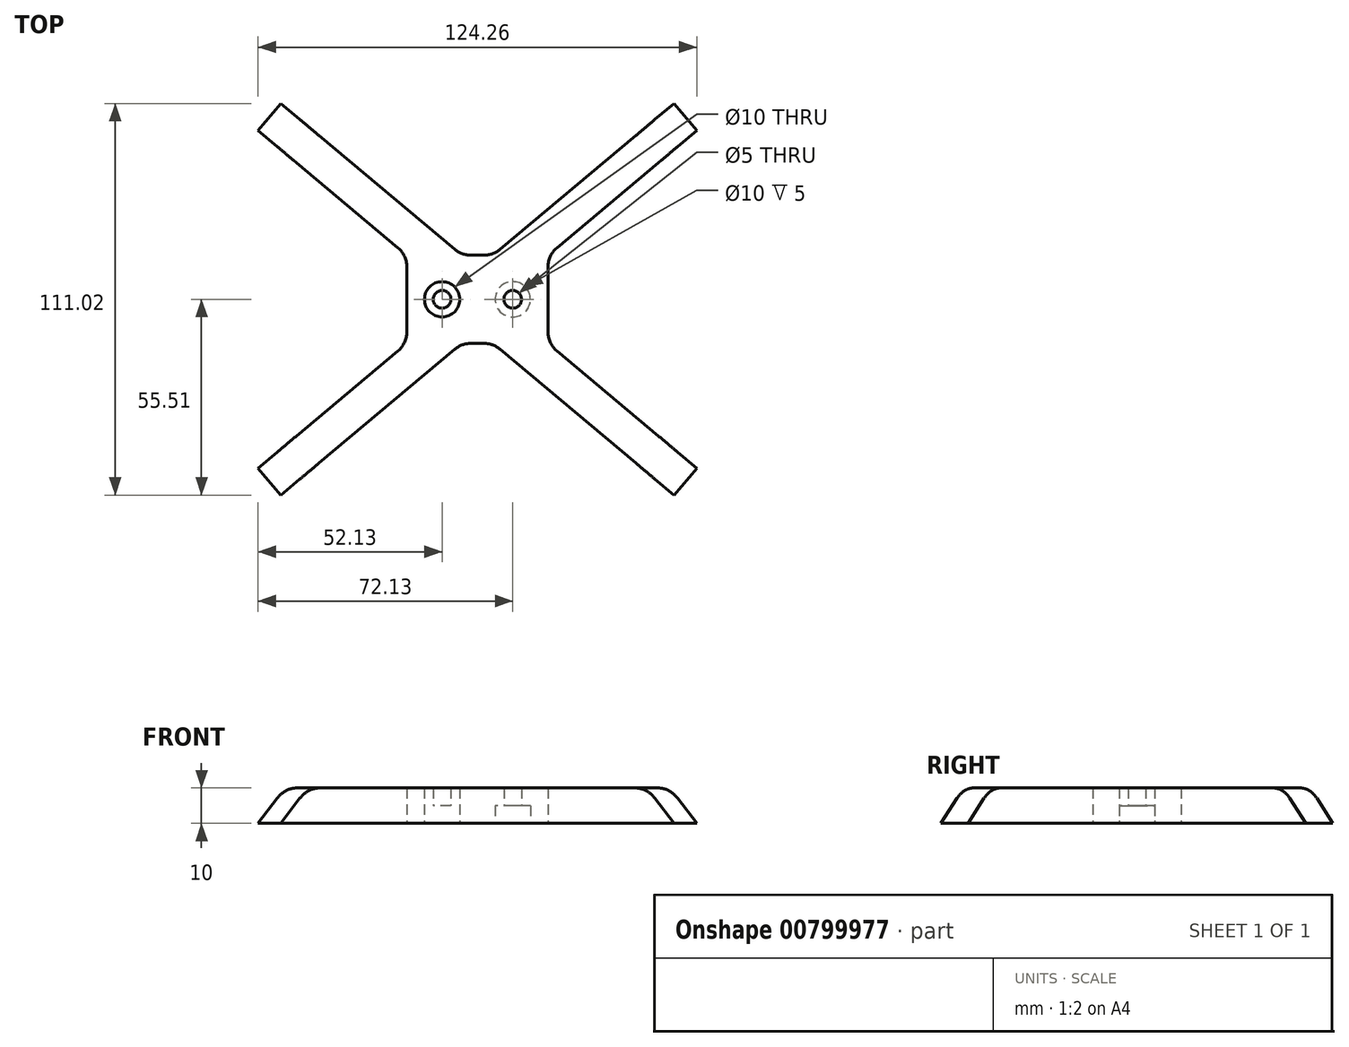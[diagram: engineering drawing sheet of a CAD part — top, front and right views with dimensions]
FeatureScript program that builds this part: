
annotation { "Feature Type Name" : "Feature", "Feature Type Description" : "" }
export const myFeature = defineFeature(function(context is Context, id is Id, definition is map)
    precondition{}
    {
        {
            var Q0;
            Q0=qCreatedBy(makeId("Top.planeOp"),FACE);
            var sketch = newSketch(context, id + "F0", { "sketchPlane" : qUnion([Q0])});
            skLineSegment(sketch, "E0.bottom", {"start": v(20, -12.5) * mm, "end": v(-20, -12.5) * mm});
            skLineSegment(sketch, "E0.top", {"start": v(20, 12.5) * mm, "end": v(-20, 12.5) * mm});
            skLineSegment(sketch, "E0.left", {"start": v(20, -12.5) * mm, "end": v(20, 12.5) * mm});
            skLineSegment(sketch, "E0.right", {"start": v(-20, -12.5) * mm, "end": v(-20, 12.5) * mm});
            skPoint(sketch, "E0.middle", {"position": v(0, 0) * mm});
            skLineSegment(sketch, "E1", {"start": v(4.44, 12.5) * mm, "end": v(55.7, 55.51) * mm});
            skLineSegment(sketch, "E2", {"start": v(55.7, 55.51) * mm, "end": v(62.13, 47.85) * mm});
            skLineSegment(sketch, "E3", {"start": v(62.13, 47.85) * mm, "end": v(20, 12.5) * mm});
            skLineSegment(sketch, "E4.MirrorCS", {"start": v(55.7, -55.51) * mm, "end": v(62.13, -47.85) * mm});
            skLineSegment(sketch, "E5.MirrorCS", {"start": v(62.13, -47.85) * mm, "end": v(20, -12.5) * mm});
            skLineSegment(sketch, "E6.MirrorCS", {"start": v(4.44, -12.5) * mm, "end": v(55.7, -55.51) * mm});
            skLineSegment(sketch, "E7.MirrorCS", {"start": v(-55.7, -55.51) * mm, "end": v(-62.13, -47.85) * mm});
            skLineSegment(sketch, "E8.MirrorCS", {"start": v(-4.44, -12.5) * mm, "end": v(-55.7, -55.51) * mm});
            skLineSegment(sketch, "E9.MirrorCS", {"start": v(-62.13, -47.85) * mm, "end": v(-20, -12.5) * mm});
            skLineSegment(sketch, "E10.MirrorCS", {"start": v(-55.7, 55.51) * mm, "end": v(-62.13, 47.85) * mm});
            skLineSegment(sketch, "E11.MirrorCS", {"start": v(-4.44, 12.5) * mm, "end": v(-55.7, 55.51) * mm});
            skLineSegment(sketch, "E12.MirrorCS", {"start": v(-62.13, 47.85) * mm, "end": v(-20, 12.5) * mm});
            skCircle(sketch, "E13", {"center": v(10, 0) * mm, "radius": 5 * mm});
            skCircle(sketch, "E14", {"center": v(10, 0) * mm, "radius": 2.5 * mm});
            skCircle(sketch, "E15.MirrorC", {"center": v(-10, 0) * mm, "radius": 2.5 * mm});
            skCircle(sketch, "E16.MirrorC", {"center": v(-10, 0) * mm, "radius": 5 * mm});
            skSolve(sketch);
        }
        {
            var Q0;
            {var subQ0=sQuery(id+"F0.wireOp",EDGE,"E0.left");Q0=makeQuery(id+"F0.imprint","IMPRINT",FACE,{"disambiguationData":[TD([[makeQuery(id+"F0.imprint","IMPRINT",EDGE,{"derivedFrom":subQ0}),1.0]])]});}
            var Q1;
            Q1=makeQuery(id+"F0.imprint","IMPRINT",FACE,{"disambiguationData":[TD([[makeQuery(id+"F0.imprint","IMPRINT",EDGE,{"derivedFrom":sQuery(id+"F0.wireOp",EDGE,"E7.MirrorCS")}),-1.0]])]});
            var Q2;
            Q2=makeQuery(id+"F0.imprint","IMPRINT",FACE,{"disambiguationData":[TD([[makeQuery(id+"F0.imprint","IMPRINT",EDGE,{"derivedFrom":sQuery(id+"F0.wireOp",EDGE,"E4.MirrorCS")}),1.0]])]});
            var Q3;
            {var subQ2=sQuery(id+"F0.wireOp",EDGE,"E1");Q3=makeQuery(id+"F0.imprint","IMPRINT",FACE,{"disambiguationData":[TD([[makeQuery(id+"F0.imprint","IMPRINT",EDGE,{"derivedFrom":subQ2}),-1.0]])]});}
            var Q4;
            Q4=makeQuery(id+"F0.imprint","IMPRINT",FACE,{"disambiguationData":[TD([[makeQuery(id+"F0.imprint","IMPRINT",EDGE,{"derivedFrom":sQuery(id+"F0.wireOp",EDGE,"E10.MirrorCS")}),1.0]])]});
            var Q5;
            Q5=makeQuery(id+"F0.imprint","IMPRINT",FACE,{"disambiguationData":[TD([[makeQuery(id+"F0.imprint","IMPRINT",EDGE,{"derivedFrom":sQuery(id+"F0.wireOp",EDGE,"E13")}),1.0]])]});
            var Q6;
            Q6=makeQuery(id+"F0.imprint","IMPRINT",FACE,{"disambiguationData":[TD([[makeQuery(id+"F0.imprint","IMPRINT",EDGE,{"derivedFrom":sQuery(id+"F0.wireOp",EDGE,"E15.MirrorC")}),1.0]])]});
            extrude(context, id + "F1", {"entities" : qUnion([Q0, Q1, Q2, Q3, Q4, Q5, Q6]), "depth" : 10 * mm, "offsetDistance" : 25 * mm});
        }
        {
            var Q0;
            Q0=makeQuery(id+"F0.imprint","IMPRINT",FACE,{"disambiguationData":[TD([[makeQuery(id+"F0.imprint","IMPRINT",EDGE,{"derivedFrom":sQuery(id+"F0.wireOp",EDGE,"E15.MirrorC")}),1.0]])]});
            var Q1;
            Q1=makeQuery(id+"F0.imprint","IMPRINT",FACE,{"disambiguationData":[TD([[makeQuery(id+"F0.imprint","IMPRINT",EDGE,{"derivedFrom":sQuery(id+"F0.wireOp",EDGE,"E13")}),1.0]])]});
            extrude(context, id + "F2", {"entities" : qUnion([Q0, Q1]), "operationType" : NewBodyOperationType.REMOVE, "depth" : 5 * mm, "offsetDistance" : 25 * mm});
        }
        {
            var Q0;
            Q0=makeQuery(id+"F1.opExtrude","CAP_EDGE",EDGE,{"disambiguationData":[OSD([sQuery(id+"F0.wireOp",EDGE,"E4.MirrorCS")])],"isStart":false});
            var Q1;
            Q1=makeQuery(id+"F1.opExtrude","CAP_EDGE",EDGE,{"disambiguationData":[OSD([sQuery(id+"F0.wireOp",EDGE,"E2")])],"isStart":false});
            var Q2;
            Q2=makeQuery(id+"F1.opExtrude","CAP_EDGE",EDGE,{"disambiguationData":[OSD([sQuery(id+"F0.wireOp",EDGE,"E10.MirrorCS")])],"isStart":false});
            var Q3;
            Q3=makeQuery(id+"F1.opExtrude","CAP_EDGE",EDGE,{"disambiguationData":[OSD([sQuery(id+"F0.wireOp",EDGE,"E7.MirrorCS")])],"isStart":false});
            chamfer(context, id + "F3", {"entities" : qUnion([Q0, Q1, Q2, Q3]), "width" : 10 * mm, "tangentPropagation" : true});
        }
        {
            var Q0;
            Q0=makeQuery(id+"F1.opExtrude","SWEPT_EDGE",EDGE,{"disambiguationData":[OSD([sQuery(id+"F0.wireOp",EDGE,"E0.top"),sQuery(id+"F0.wireOp",EDGE,"E1")])]});
            var Q1;
            Q1=makeQuery(id+"F1.opExtrude","SWEPT_EDGE",EDGE,{"disambiguationData":[OSD([sQuery(id+"F0.wireOp",EDGE,"E0.top"),sQuery(id+"F0.wireOp",EDGE,"E11.MirrorCS")])]});
            var Q2;
            Q2=makeQuery(id+"F1.opExtrude","SWEPT_EDGE",EDGE,{"disambiguationData":[OSD([sQuery(id+"F0.wireOp",EDGE,"E0.bottom"),sQuery(id+"F0.wireOp",EDGE,"E6.MirrorCS")])]});
            var Q3;
            Q3=makeQuery(id+"F1.opExtrude","SWEPT_EDGE",EDGE,{"disambiguationData":[OSD([sQuery(id+"F0.wireOp",EDGE,"E0.bottom"),sQuery(id+"F0.wireOp",EDGE,"E8.MirrorCS")])]});
            var Q4;
            Q4=makeQuery(id+"F1.opExtrude","SWEPT_EDGE",EDGE,{"disambiguationData":[OSD([sQuery(id+"F0.wireOp",EDGE,"E0.bottom"),sQuery(id+"F0.wireOp",EDGE,"E0.right"),sQuery(id+"F0.wireOp",EDGE,"E9.MirrorCS")])]});
            var Q5;
            Q5=makeQuery(id+"F1.opExtrude","SWEPT_EDGE",EDGE,{"disambiguationData":[OSD([sQuery(id+"F0.wireOp",EDGE,"E0.top"),sQuery(id+"F0.wireOp",EDGE,"E0.right"),sQuery(id+"F0.wireOp",EDGE,"E12.MirrorCS")])]});
            var Q6;
            Q6=makeQuery(id+"F1.opExtrude","SWEPT_EDGE",EDGE,{"disambiguationData":[OSD([sQuery(id+"F0.wireOp",EDGE,"E0.bottom"),sQuery(id+"F0.wireOp",EDGE,"E0.left"),sQuery(id+"F0.wireOp",EDGE,"E5.MirrorCS")])]});
            var Q7;
            Q7=makeQuery(id+"F1.opExtrude","SWEPT_EDGE",EDGE,{"disambiguationData":[OSD([sQuery(id+"F0.wireOp",EDGE,"E0.top"),sQuery(id+"F0.wireOp",EDGE,"E0.left"),sQuery(id+"F0.wireOp",EDGE,"E3")])]});
            fillet(context, id + "F4", {"entities" : qUnion([Q0, Q1, Q2, Q3, Q4, Q5, Q6, Q7]), "radius" : 7 * mm, "tangentPropagation" : true, "allowEdgeOverflow" : false});
        }
        {
            var Q0;
            {var subQ0=sQuery(id+"F0.wireOp",EDGE,"E10.MirrorCS");Q0=makeQuery(id+"F3.opChamfer","BLEND_EDGE",EDGE,{"blendedFrom":[makeQuery(id+"F1.opExtrude","CAP_EDGE",EDGE,{"disambiguationData":[OSD([subQ0])],"isStart":false}),makeQuery(id+"F1.opExtrude","CAP_FACE",FACE,{"disambiguationData":[OSD([sQuery(id+"F0.wireOp",EDGE,"E0.bottom"),sQuery(id+"F0.wireOp",EDGE,"E0.top"),sQuery(id+"F0.wireOp",EDGE,"E0.left"),sQuery(id+"F0.wireOp",EDGE,"E0.right"),sQuery(id+"F0.wireOp",EDGE,"E1"),sQuery(id+"F0.wireOp",EDGE,"E2"),sQuery(id+"F0.wireOp",EDGE,"E3"),sQuery(id+"F0.wireOp",EDGE,"E4.MirrorCS"),sQuery(id+"F0.wireOp",EDGE,"E5.MirrorCS"),sQuery(id+"F0.wireOp",EDGE,"E6.MirrorCS"),sQuery(id+"F0.wireOp",EDGE,"E7.MirrorCS"),sQuery(id+"F0.wireOp",EDGE,"E8.MirrorCS"),sQuery(id+"F0.wireOp",EDGE,"E9.MirrorCS"),subQ0,sQuery(id+"F0.wireOp",EDGE,"E11.MirrorCS"),sQuery(id+"F0.wireOp",EDGE,"E12.MirrorCS"),sQuery(id+"F0.wireOp",EDGE,"E14"),sQuery(id+"F0.wireOp",EDGE,"E15.MirrorC")])],"isStart":false})],"blendedInto":[makeQuery(id+"F1.opExtrude","CAP_FACE",FACE,{"disambiguationData":[OSD([sQuery(id+"F0.wireOp",EDGE,"E0.bottom"),sQuery(id+"F0.wireOp",EDGE,"E0.top"),sQuery(id+"F0.wireOp",EDGE,"E0.left"),sQuery(id+"F0.wireOp",EDGE,"E0.right"),sQuery(id+"F0.wireOp",EDGE,"E1"),sQuery(id+"F0.wireOp",EDGE,"E2"),sQuery(id+"F0.wireOp",EDGE,"E3"),sQuery(id+"F0.wireOp",EDGE,"E4.MirrorCS"),sQuery(id+"F0.wireOp",EDGE,"E5.MirrorCS"),sQuery(id+"F0.wireOp",EDGE,"E6.MirrorCS"),sQuery(id+"F0.wireOp",EDGE,"E7.MirrorCS"),sQuery(id+"F0.wireOp",EDGE,"E8.MirrorCS"),sQuery(id+"F0.wireOp",EDGE,"E9.MirrorCS"),subQ0,sQuery(id+"F0.wireOp",EDGE,"E11.MirrorCS"),sQuery(id+"F0.wireOp",EDGE,"E12.MirrorCS"),sQuery(id+"F0.wireOp",EDGE,"E14"),sQuery(id+"F0.wireOp",EDGE,"E15.MirrorC")])],"isStart":false})]});}
            var Q1;
            {var subQ0=sQuery(id+"F0.wireOp",EDGE,"E7.MirrorCS");Q1=makeQuery(id+"F3.opChamfer","BLEND_EDGE",EDGE,{"blendedFrom":[makeQuery(id+"F1.opExtrude","CAP_EDGE",EDGE,{"disambiguationData":[OSD([subQ0])],"isStart":false}),makeQuery(id+"F1.opExtrude","CAP_FACE",FACE,{"disambiguationData":[OSD([sQuery(id+"F0.wireOp",EDGE,"E0.bottom"),sQuery(id+"F0.wireOp",EDGE,"E0.top"),sQuery(id+"F0.wireOp",EDGE,"E0.left"),sQuery(id+"F0.wireOp",EDGE,"E0.right"),sQuery(id+"F0.wireOp",EDGE,"E1"),sQuery(id+"F0.wireOp",EDGE,"E2"),sQuery(id+"F0.wireOp",EDGE,"E3"),sQuery(id+"F0.wireOp",EDGE,"E4.MirrorCS"),sQuery(id+"F0.wireOp",EDGE,"E5.MirrorCS"),sQuery(id+"F0.wireOp",EDGE,"E6.MirrorCS"),subQ0,sQuery(id+"F0.wireOp",EDGE,"E8.MirrorCS"),sQuery(id+"F0.wireOp",EDGE,"E9.MirrorCS"),sQuery(id+"F0.wireOp",EDGE,"E10.MirrorCS"),sQuery(id+"F0.wireOp",EDGE,"E11.MirrorCS"),sQuery(id+"F0.wireOp",EDGE,"E12.MirrorCS"),sQuery(id+"F0.wireOp",EDGE,"E14"),sQuery(id+"F0.wireOp",EDGE,"E15.MirrorC")])],"isStart":false})],"blendedInto":[makeQuery(id+"F1.opExtrude","CAP_FACE",FACE,{"disambiguationData":[OSD([sQuery(id+"F0.wireOp",EDGE,"E0.bottom"),sQuery(id+"F0.wireOp",EDGE,"E0.top"),sQuery(id+"F0.wireOp",EDGE,"E0.left"),sQuery(id+"F0.wireOp",EDGE,"E0.right"),sQuery(id+"F0.wireOp",EDGE,"E1"),sQuery(id+"F0.wireOp",EDGE,"E2"),sQuery(id+"F0.wireOp",EDGE,"E3"),sQuery(id+"F0.wireOp",EDGE,"E4.MirrorCS"),sQuery(id+"F0.wireOp",EDGE,"E5.MirrorCS"),sQuery(id+"F0.wireOp",EDGE,"E6.MirrorCS"),subQ0,sQuery(id+"F0.wireOp",EDGE,"E8.MirrorCS"),sQuery(id+"F0.wireOp",EDGE,"E9.MirrorCS"),sQuery(id+"F0.wireOp",EDGE,"E10.MirrorCS"),sQuery(id+"F0.wireOp",EDGE,"E11.MirrorCS"),sQuery(id+"F0.wireOp",EDGE,"E12.MirrorCS"),sQuery(id+"F0.wireOp",EDGE,"E14"),sQuery(id+"F0.wireOp",EDGE,"E15.MirrorC")])],"isStart":false})]});}
            var Q2;
            {var subQ0=sQuery(id+"F0.wireOp",EDGE,"E2");Q2=makeQuery(id+"F3.opChamfer","BLEND_EDGE",EDGE,{"blendedFrom":[makeQuery(id+"F1.opExtrude","CAP_EDGE",EDGE,{"disambiguationData":[OSD([subQ0])],"isStart":false}),makeQuery(id+"F1.opExtrude","CAP_FACE",FACE,{"disambiguationData":[OSD([sQuery(id+"F0.wireOp",EDGE,"E0.bottom"),sQuery(id+"F0.wireOp",EDGE,"E0.top"),sQuery(id+"F0.wireOp",EDGE,"E0.left"),sQuery(id+"F0.wireOp",EDGE,"E0.right"),sQuery(id+"F0.wireOp",EDGE,"E1"),subQ0,sQuery(id+"F0.wireOp",EDGE,"E3"),sQuery(id+"F0.wireOp",EDGE,"E4.MirrorCS"),sQuery(id+"F0.wireOp",EDGE,"E5.MirrorCS"),sQuery(id+"F0.wireOp",EDGE,"E6.MirrorCS"),sQuery(id+"F0.wireOp",EDGE,"E7.MirrorCS"),sQuery(id+"F0.wireOp",EDGE,"E8.MirrorCS"),sQuery(id+"F0.wireOp",EDGE,"E9.MirrorCS"),sQuery(id+"F0.wireOp",EDGE,"E10.MirrorCS"),sQuery(id+"F0.wireOp",EDGE,"E11.MirrorCS"),sQuery(id+"F0.wireOp",EDGE,"E12.MirrorCS"),sQuery(id+"F0.wireOp",EDGE,"E14"),sQuery(id+"F0.wireOp",EDGE,"E15.MirrorC")])],"isStart":false})],"blendedInto":[makeQuery(id+"F1.opExtrude","CAP_FACE",FACE,{"disambiguationData":[OSD([sQuery(id+"F0.wireOp",EDGE,"E0.bottom"),sQuery(id+"F0.wireOp",EDGE,"E0.top"),sQuery(id+"F0.wireOp",EDGE,"E0.left"),sQuery(id+"F0.wireOp",EDGE,"E0.right"),sQuery(id+"F0.wireOp",EDGE,"E1"),subQ0,sQuery(id+"F0.wireOp",EDGE,"E3"),sQuery(id+"F0.wireOp",EDGE,"E4.MirrorCS"),sQuery(id+"F0.wireOp",EDGE,"E5.MirrorCS"),sQuery(id+"F0.wireOp",EDGE,"E6.MirrorCS"),sQuery(id+"F0.wireOp",EDGE,"E7.MirrorCS"),sQuery(id+"F0.wireOp",EDGE,"E8.MirrorCS"),sQuery(id+"F0.wireOp",EDGE,"E9.MirrorCS"),sQuery(id+"F0.wireOp",EDGE,"E10.MirrorCS"),sQuery(id+"F0.wireOp",EDGE,"E11.MirrorCS"),sQuery(id+"F0.wireOp",EDGE,"E12.MirrorCS"),sQuery(id+"F0.wireOp",EDGE,"E14"),sQuery(id+"F0.wireOp",EDGE,"E15.MirrorC")])],"isStart":false})]});}
            var Q3;
            {var subQ0=sQuery(id+"F0.wireOp",EDGE,"E4.MirrorCS");Q3=makeQuery(id+"F3.opChamfer","BLEND_EDGE",EDGE,{"blendedFrom":[makeQuery(id+"F1.opExtrude","CAP_EDGE",EDGE,{"disambiguationData":[OSD([subQ0])],"isStart":false}),makeQuery(id+"F1.opExtrude","CAP_FACE",FACE,{"disambiguationData":[OSD([sQuery(id+"F0.wireOp",EDGE,"E0.bottom"),sQuery(id+"F0.wireOp",EDGE,"E0.top"),sQuery(id+"F0.wireOp",EDGE,"E0.left"),sQuery(id+"F0.wireOp",EDGE,"E0.right"),sQuery(id+"F0.wireOp",EDGE,"E1"),sQuery(id+"F0.wireOp",EDGE,"E2"),sQuery(id+"F0.wireOp",EDGE,"E3"),subQ0,sQuery(id+"F0.wireOp",EDGE,"E5.MirrorCS"),sQuery(id+"F0.wireOp",EDGE,"E6.MirrorCS"),sQuery(id+"F0.wireOp",EDGE,"E7.MirrorCS"),sQuery(id+"F0.wireOp",EDGE,"E8.MirrorCS"),sQuery(id+"F0.wireOp",EDGE,"E9.MirrorCS"),sQuery(id+"F0.wireOp",EDGE,"E10.MirrorCS"),sQuery(id+"F0.wireOp",EDGE,"E11.MirrorCS"),sQuery(id+"F0.wireOp",EDGE,"E12.MirrorCS"),sQuery(id+"F0.wireOp",EDGE,"E14"),sQuery(id+"F0.wireOp",EDGE,"E15.MirrorC")])],"isStart":false})],"blendedInto":[makeQuery(id+"F1.opExtrude","CAP_FACE",FACE,{"disambiguationData":[OSD([sQuery(id+"F0.wireOp",EDGE,"E0.bottom"),sQuery(id+"F0.wireOp",EDGE,"E0.top"),sQuery(id+"F0.wireOp",EDGE,"E0.left"),sQuery(id+"F0.wireOp",EDGE,"E0.right"),sQuery(id+"F0.wireOp",EDGE,"E1"),sQuery(id+"F0.wireOp",EDGE,"E2"),sQuery(id+"F0.wireOp",EDGE,"E3"),subQ0,sQuery(id+"F0.wireOp",EDGE,"E5.MirrorCS"),sQuery(id+"F0.wireOp",EDGE,"E6.MirrorCS"),sQuery(id+"F0.wireOp",EDGE,"E7.MirrorCS"),sQuery(id+"F0.wireOp",EDGE,"E8.MirrorCS"),sQuery(id+"F0.wireOp",EDGE,"E9.MirrorCS"),sQuery(id+"F0.wireOp",EDGE,"E10.MirrorCS"),sQuery(id+"F0.wireOp",EDGE,"E11.MirrorCS"),sQuery(id+"F0.wireOp",EDGE,"E12.MirrorCS"),sQuery(id+"F0.wireOp",EDGE,"E14"),sQuery(id+"F0.wireOp",EDGE,"E15.MirrorC")])],"isStart":false})]});}
            fillet(context, id + "F5", {"entities" : qUnion([Q0, Q1, Q2, Q3]), "radius" : 10 * mm, "tangentPropagation" : true, "allowEdgeOverflow" : false});
        }
    });
